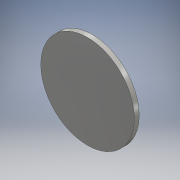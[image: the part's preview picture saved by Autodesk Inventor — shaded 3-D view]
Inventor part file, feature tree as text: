
AUTODESK INVENTOR PART (.ipt)
format: ipt  version: 2016 (Build 200138000, 138)  size: 101,376 bytes
history: native  units: mm
features: extrude x1, sketch x1
ambient origin geometry x8: Origin, YZ Plane, XZ Plane, XY Plane, X Axis, Y Axis, Z Axis, Center Point
bodies: Solid1 (feature_tree)
feature tree (2):
  extrude  "Extrusion1"  Depth=3.0mm TaperAngle=0.0deg
  sketch  "Sketch1"  dims[d0=57.5mm d1=3.0mm d2=0.0mm]
